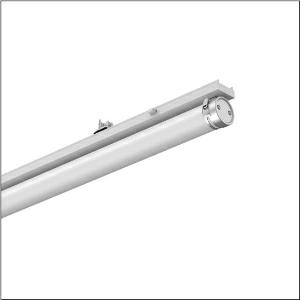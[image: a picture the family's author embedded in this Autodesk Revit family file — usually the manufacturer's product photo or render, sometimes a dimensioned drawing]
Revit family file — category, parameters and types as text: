
# Revit family: monsun_r__31_tube_51ft10nn4a0atr2_f2a8
name_source: partatom
category: Lighting Fixtures
units: mm (PartAtom-declared; Revit-internal decimal feet)

## family parameters
Cut with Voids When Loaded = No
Host = Face
Light Source = No
Part Type = Normal
Room Calculation Point = No
Round Connector Dimension = Use Diameter
Shared = No

## types (1)
- --- (1 x LED, 10000 lm, 58 W, 4000K)
    Apparent Load = 58 VA
    CIE Flux Codes = 42 71 90 91 100
    Color Rendering = 80
    Color Temperature = 4000K
    Default Elevation = 1800 mm
    Description = Monsun® 31 Tube, tubular luminaire, primary optical cover: diffuser, of PMMA, light emission: direct distribution, primary light characteristic: symmetric, LED, rated luminous flux: 10.000lm, luminous efficacy: 172lm/W, light colour: 840, colour temperature: 4000K, with with 1 terminal, 5-pole, max. 2.5mm², mains connection: 220..240V, AC, 50/60Hz, rated input power: 58W, housing, cylindrical, of PMMA, semi-transparent, matt white, with luminaire and ceiling fastening, V4A, mounting with brackets of stainless steel, length: 1.500mm, diameter: 75mm, end cap, of stainless steel (V4A), protection rating (complete): IP20, protection rating (lamp compartment): IP67/69K, insulation class (complete): insulation class I (protective earthing), certification: CE, UKCA, impact resistance: IK06, permissible operating ambient temperature: -20..+40°C, corresponds to IFS (International Featured Standards) requirements for safety and quality in the food industry, contact your sales advisor before using the luminaires in applications with unclear chemical exposure, large temperature fluctuations or condensation-forming humidity, packaging unit: 1 piece
    Height = 132 mm
    Lamp = 1 x LED
    Lamp Light Flux = 10000 lm
    Lamp Power = 58 W
    Lamp count = 1
    Length = 1500 mm
    Luminous efficacy = 172 lm/W
    Manufacturer = Siteco
    ModVariant = No
    Model = 51FT10NN4A0ATR2
    Mounting Place = Ceiling
    Mounting Type = Pendant
    Number of Poles = 1
    OnlyDefault = Yes
    Power Factor = 1
    Product Name = Monsun® 31 Tube
    Product group = tubular luminaire
    ProductGroupID = 906
    Protection Class = Protection class I
    Protection Degree = IP 20
    RLX_Detail_Level = 1
    RLX_Emergency_Light_Flux = 0 lm
    RLX_Emergency_Type = 0
    RLX_Emergency_Type_DB = No
    RlxData = <blob elided: 32341 chars, md5=0d13d5c0>
    Socket = socket
    Standby Power = 0 W
    System Light Flux = 10000 lm
    System Power = 58 W
    Type Comments = individual setting: luminous flux: 100 % | (OFF | OFF | ON | OFF) | 350 mA
    Type Image = l_1242814.jpg
    URL = http://relux.com
    VarID = @adj_092723
    Voltage = 0 V
    Weight = 0.00 kg
    Width = 79 mm

## geometry (parser evidence)
native form markers: Blend x4, Sweep x10
no freeform markers — native parametric forms only
